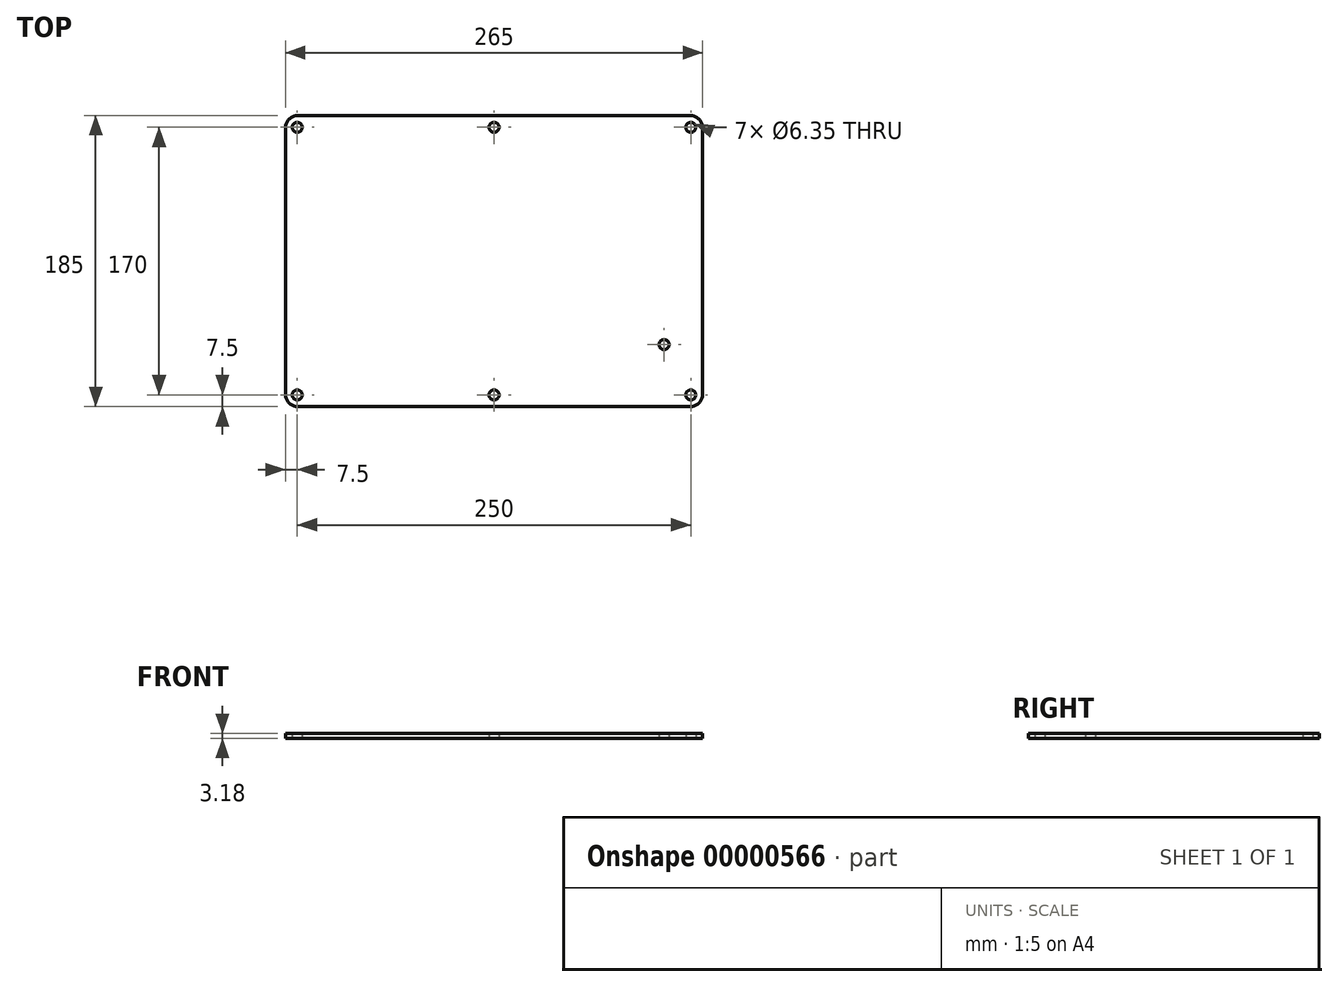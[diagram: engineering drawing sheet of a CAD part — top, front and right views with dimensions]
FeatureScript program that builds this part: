
annotation { "Feature Type Name" : "Feature", "Feature Type Description" : "" }
export const myFeature = defineFeature(function(context is Context, id is Id, definition is map)
    precondition{}
    {
        {
            var Q0;
            Q0=qCreatedBy(makeId("Top.planeOp"),FACE);
            var sketch = newSketch(context, id + "F0", { "sketchPlane" : qUnion([Q0])});
            skLineSegment(sketch, "E0.rect.bottom", {"start": v(-132.5, 92.5) * mm, "end": v(132.5, 92.5) * mm});
            skLineSegment(sketch, "E0.rect.top", {"start": v(-132.5, -92.5) * mm, "end": v(132.5, -92.5) * mm});
            skLineSegment(sketch, "E0.rect.left", {"start": v(-132.5, 92.5) * mm, "end": v(-132.5, -92.5) * mm});
            skLineSegment(sketch, "E0.rect.right", {"start": v(132.5, 92.5) * mm, "end": v(132.5, -92.5) * mm});
            skPoint(sketch, "E0.rect.middle", {"position": v(0, 0) * mm});
            skCircle(sketch, "E1", {"center": v(0, 85) * mm, "radius": 3.18 * mm});
            skLineSegment(sketch, "E2", {"start": v(0, 0) * mm, "end": v(-132.5, 0) * mm, "construction": true});
            skLineSegment(sketch, "E3", {"start": v(0, 0) * mm, "end": v(0, 92.5) * mm, "construction": true});
            skCircle(sketch, "E4", {"center": v(-125, 85) * mm, "radius": 3.18 * mm});
            skCircle(sketch, "E5.0.MirrorC", {"center": v(125, 85) * mm, "radius": 3.18 * mm});
            skCircle(sketch, "E6.0.MirrorC", {"center": v(0, -85) * mm, "radius": 3.18 * mm});
            skCircle(sketch, "E7.0.MirrorC", {"center": v(-125, -85) * mm, "radius": 3.18 * mm});
            skCircle(sketch, "E8.0.MirrorC", {"center": v(125, -85) * mm, "radius": 3.18 * mm});
            skCircle(sketch, "E9", {"center": v(108.02, -53.02) * mm, "radius": 3.18 * mm});
            skSolve(sketch);
        }
        {
            var Q0;
            Q0 = qSketchRegion(id + "F0", true);
            extrude(context, id + "F1", {"entities" : qUnion([Q0]), "depth" : 3.17 * mm});
        }
        {
            var Q0;
            Q0=makeQuery(id+"F1.opExtrude","SWEPT_EDGE",EDGE,{"disambiguationData":[OSD([sQuery(id+"F0.wireOp",EDGE,"E0.rect.bottom"),sQuery(id+"F0.wireOp",EDGE,"E0.rect.left")])]});
            var Q1;
            Q1=makeQuery(id+"F1.opExtrude","SWEPT_EDGE",EDGE,{"disambiguationData":[OSD([sQuery(id+"F0.wireOp",EDGE,"E0.rect.bottom"),sQuery(id+"F0.wireOp",EDGE,"E0.rect.right")])]});
            var Q2;
            Q2=makeQuery(id+"F1.opExtrude","SWEPT_EDGE",EDGE,{"disambiguationData":[OSD([sQuery(id+"F0.wireOp",EDGE,"E0.rect.top"),sQuery(id+"F0.wireOp",EDGE,"E0.rect.right")])]});
            var Q3;
            Q3=makeQuery(id+"F1.opExtrude","SWEPT_EDGE",EDGE,{"disambiguationData":[OSD([sQuery(id+"F0.wireOp",EDGE,"E0.rect.top"),sQuery(id+"F0.wireOp",EDGE,"E0.rect.left")])]});
            fillet(context, id + "F2", {"entities" : qUnion([Q0, Q1, Q2, Q3]), "radius" : 8 * mm, "tangentPropagation" : true, "allowEdgeOverflow" : false});
        }
    });
